# Revit family: HCSREC
name_source: partatom
category: Communication Devices
revit_build: Autodesk Revit 2014 (Build: 20130308_1515(x64)
units: mm (PartAtom-declared; Revit-internal decimal feet)

## types (1)
- HCSREC
    Assembly Code = D5090
    Certifications = cUL 498B SA Fed. Spec. WC596G
    Connecting Metal = Hubbell- Meta - Gold
    Default Elevation = 48 "
    Description = The Hubbell Control Solutions (HCS) Duplex Receptacle is the latest addition
to the HCS comprehensive offering for controlled devices. Featuring Hubbell’s
exclusive and patented tamper-resistant mechanism, the unit is capable of
controlling other receptacles downstream in the branch circuit. Hubbell offers
this innovative device in a wired control option. The series is designed to be
automatically controlled by a low voltage signal from occupancy sensors or
any other type of control capable of performing this task, such as a time-ofday
control device. This controlled receptacle solution is fully compatible with
existing systems.
    Feartures = Split or Fully Controlled 15A or 20A Options
• Downstream Branch Circuit Control
• Permanent NEC 406.3 (E) Markings
• UL498B SA Listed Receptacles with Integral Switching Comply with
Supplement SA
• Fed Spec W596G
    Housing Material = Paint - Hubbell - Matte White
    Manufacturer = Hubbell Control Solutions
    Model = HCSREC Series
    Product Documentation Link = https://hubbellcdn.com
    Product Page URL = https://www.hubbell.com
    Support = Paint - Hubbell - Carbon Black
    Type Comments = Controlled Receptacle
    URL = https://www.hubbell.com
    Warranty = 5-Years Warranty

## geometry (parser evidence)
native form markers: Sweep x2
no freeform markers — native parametric forms only
